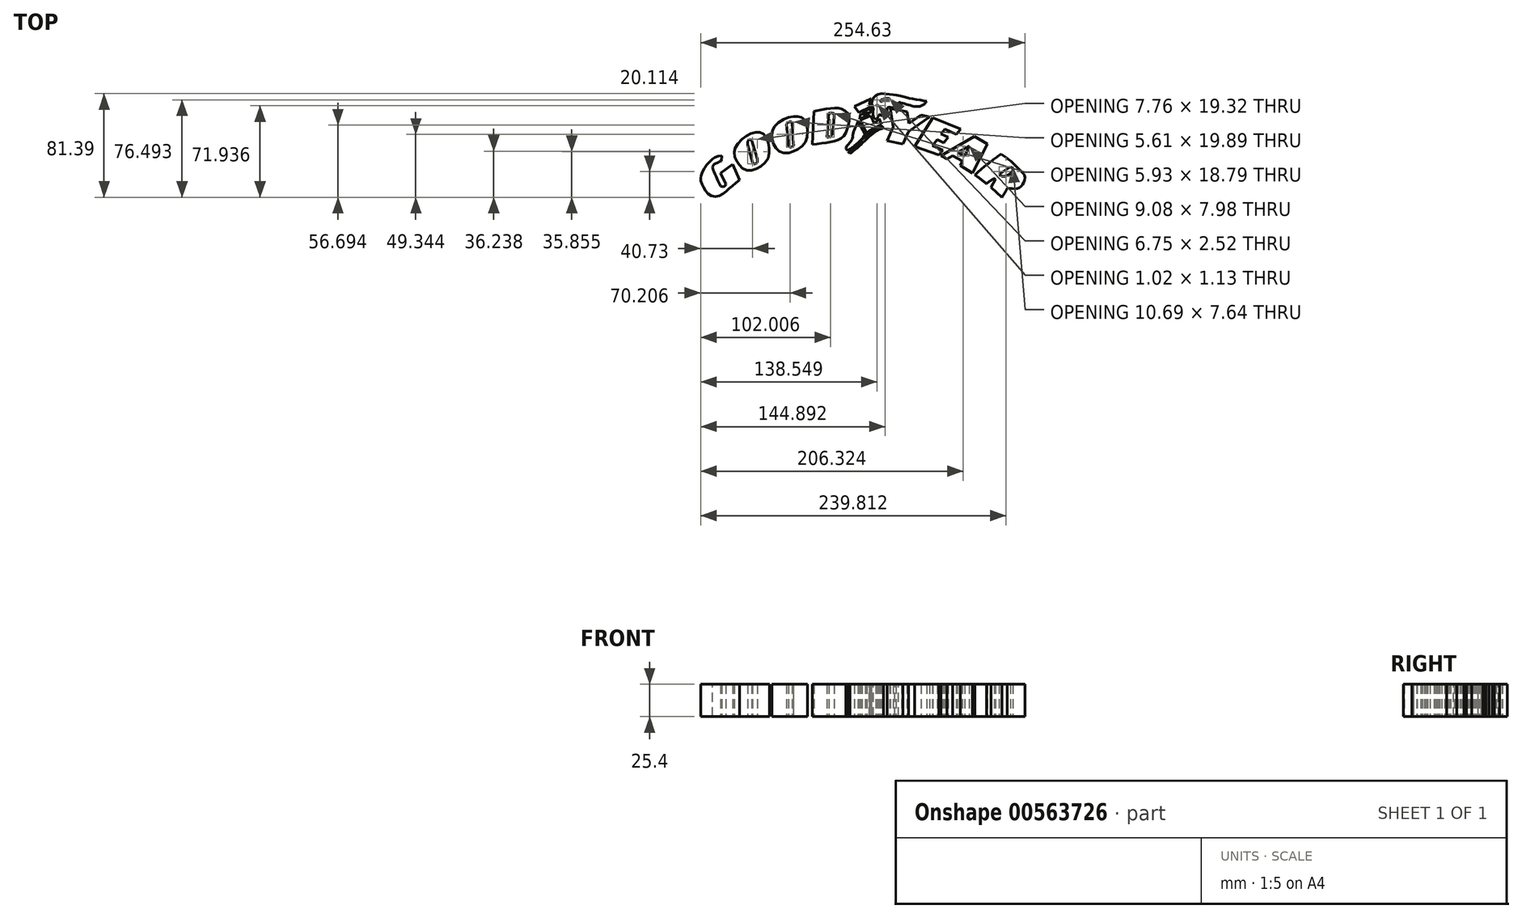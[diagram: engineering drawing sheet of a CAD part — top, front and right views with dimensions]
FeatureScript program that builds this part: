
annotation { "Feature Type Name" : "Feature", "Feature Type Description" : "" }
export const myFeature = defineFeature(function(context is Context, id is Id, definition is map)
    precondition{}
    {
        {
            var Q0;
            Q0=qCreatedBy(makeId("Top.planeOp"),FACE);
            var sketch = newSketch(context, id + "F0", { "sketchPlane" : qUnion([Q0])});
            skFitSpline(sketch, "E0", {"points": [v(-59.77, 19.65) * mm, v(-63.83, 18.9) * mm, v(-66.56, 17.29) * mm, v(-70.08, 14) * mm, v(-73.2, 9.83) * mm, v(-75.73, 4.75) * mm, v(-76.25, 2.47) * mm, v(-76.18, 0) * mm, v(-74.98, -3.55) * mm, v(-72.37, -7.96) * mm, v(-69.17, -11.16) * mm, v(-64.56, -12.56) * mm, v(-59.15, -10.76) * mm, v(-55.35, -7.59) * mm, v(-51.14, -3.95) * mm, v(-45.8, 0.36) * mm], "startDerivative": vector(-48.72, 2.07) * mm, "endDerivative": vector(63.75, 50.3) * mm});
            skLineSegment(sketch, "E1", {"start": v(-59.77, 19.65) * mm, "end": v(-59.86, 15.48) * mm});
            skLineSegment(sketch, "E2", {"start": v(-45.8, 0.36) * mm, "end": v(-51.25, 12.96) * mm});
            skLineSegment(sketch, "E3", {"start": v(-51.25, 12.96) * mm, "end": v(-60.63, 5.88) * mm});
            skLineSegment(sketch, "E4", {"start": v(-60.63, 5.88) * mm, "end": v(-56.41, -2.7) * mm});
            skFitSpline(sketch, "E5", {"points": [v(-59.86, 15.48) * mm, v(-62.4, 14.45) * mm, v(-64.42, 13.43) * mm, v(-66.28, 12.15) * mm, v(-66.87, 9.93) * mm, v(-66.03, 7.47) * mm, v(-64, 2.8) * mm, v(-62.32, -0.84) * mm, v(-61.06, -3.39) * mm, v(-60.55, -4.32) * mm, v(-58.95, -4.91) * mm, v(-57.09, -4.06) * mm, v(-56.41, -2.7) * mm], "startDerivative": vector(-29.78, -11.35) * mm, "endDerivative": vector(6.97, 21.82) * mm});
            skFitSpline(sketch, "E6", {"points": [v(-49.9, 22.3) * mm, v(-48.7, 26.42) * mm, v(-44.08, 32.4) * mm, v(-38.41, 36.27) * mm, v(-33.27, 38.01) * mm, v(-29.32, 37.9) * mm, v(-25.5, 35.12) * mm, v(-23.13, 29.56) * mm, v(-22.34, 23.86) * mm, v(-23.27, 17.75) * mm, v(-27.62, 12.43) * mm, v(-32.9, 9.1) * mm, v(-38.3, 7.89) * mm, v(-43.44, 9.73) * mm, v(-46.87, 13.56) * mm, v(-48.97, 17.14) * mm, v(-49.9, 22.3) * mm]});
            skLineSegment(sketch, "E7", {"start": v(-36.05, 31.72) * mm, "end": v(-31.85, 16.84) * mm});
            skLineSegment(sketch, "E8", {"start": v(-39.36, 28.04) * mm, "end": v(-35.4, 14.58) * mm});
            skFitSpline(sketch, "E9", {"points": [v(-39.36, 28.04) * mm, v(-39.36, 30.3) * mm, v(-38.28, 31.96) * mm, v(-36.88, 32.38) * mm, v(-36.05, 31.72) * mm], "startDerivative": vector(-0.89, 7.93) * mm, "endDerivative": vector(3.61, -4.33) * mm});
            skFitSpline(sketch, "E10", {"points": [v(-31.85, 16.84) * mm, v(-31.85, 14.17) * mm, v(-33.09, 13.34) * mm, v(-34.41, 13.08) * mm, v(-35.4, 14.58) * mm], "startDerivative": vector(1.44, -10.29) * mm, "endDerivative": vector(-1.3, 7.85) * mm});
            skLineSegment(sketch, "E11", {"start": v(-8.9, 44.2) * mm, "end": v(-7.35, 27.45) * mm});
            skLineSegment(sketch, "E12", {"start": v(-4.4, 45.2) * mm, "end": v(-3.4, 28.77) * mm});
            skFitSpline(sketch, "E13", {"points": [v(-8.9, 44.2) * mm, v(-8.13, 45.2) * mm, v(-6.65, 46.05) * mm, v(-5.18, 46.05) * mm, v(-4.4, 45.2) * mm], "startDerivative": vector(2.8, 4.36) * mm, "endDerivative": vector(2.83, -4.51) * mm});
            skFitSpline(sketch, "E14", {"points": [v(-7.35, 27.45) * mm, v(-6.5, 26.52) * mm, v(-5.65, 26.29) * mm, v(-4.64, 26.44) * mm, v(-3.4, 27.3) * mm, v(-3.4, 28.77) * mm], "startDerivative": vector(3.78, -5) * mm, "endDerivative": vector(-0.95, 4.32) * mm});
            skFitSpline(sketch, "E15", {"points": [v(-18.2, 42.64) * mm, v(-12.62, 47.37) * mm, v(-6.27, 49.93) * mm, v(-1.3, 50.4) * mm, v(2.34, 49.85) * mm, v(5.9, 47.3) * mm, v(7.53, 39.7) * mm, v(6.83, 32.33) * mm, v(4.12, 27.53) * mm, v(-1.46, 23.89) * mm, v(-6.11, 21.87) * mm, v(-12.23, 22.1) * mm, v(-16.34, 24.5) * mm, v(-18.82, 28.46) * mm, v(-20.22, 33.88) * mm, v(-19.9, 39.39) * mm, v(-18.2, 42.64) * mm]});
            skLineSegment(sketch, "E16", {"start": v(11.4, 28.26) * mm, "end": v(12.75, 54.33) * mm});
            skFitSpline(sketch, "E17", {"points": [v(12.75, 54.33) * mm, v(20.03, 55.86) * mm, v(28.5, 57.04) * mm, v(34.08, 56.36) * mm, v(39.5, 52.64) * mm, v(40.17, 45.53) * mm, v(38.14, 38.42) * mm, v(34.59, 33.68) * mm, v(28.83, 31.14) * mm, v(21.05, 29.62) * mm, v(11.4, 28.26) * mm], "startDerivative": vector(68.9, 15.11) * mm, "endDerivative": vector(-84.89, -11.4) * mm});
            skLineSegment(sketch, "E18", {"start": v(24.6, 52.98) * mm, "end": v(22.74, 34.19) * mm});
            skFitSpline(sketch, "E19", {"points": [v(24.6, 52.98) * mm, v(27.14, 52.98) * mm, v(28.44, 52.5) * mm, v(28.64, 50.15) * mm, v(27.66, 41.03) * mm, v(26.74, 36.1) * mm, v(26.16, 35.14) * mm, v(25.17, 34.46) * mm, v(22.74, 34.19) * mm], "startDerivative": vector(22.33, 0.87) * mm, "endDerivative": vector(-23, -0.54) * mm});
            skFitSpline(sketch, "E20", {"points": [v(39.1, 23.6) * mm, v(44.18, 27) * mm, v(48.7, 31.12) * mm, v(50.89, 33.22) * mm, v(51.7, 34.88) * mm, v(52.92, 36) * mm], "startDerivative": vector(19.7, 11.7) * mm, "endDerivative": vector(13.38, 3.84) * mm});
            skLineSegment(sketch, "E21", {"start": v(47.46, 46.57) * mm, "end": v(52.92, 36) * mm});
            skFitSpline(sketch, "E22", {"points": [v(47.46, 46.57) * mm, v(46.54, 44.19) * mm, v(45.11, 41.5) * mm, v(43.53, 37) * mm, v(42.43, 32.07) * mm, v(39.8, 28.44) * mm, v(38.07, 26.31) * mm, v(37.96, 24.84) * mm, v(39.1, 23.6) * mm], "startDerivative": vector(-7.2, -21.21) * mm, "endDerivative": vector(15.31, -12.42) * mm});
            skLineSegment(sketch, "E23", {"start": v(40.96, 21.31) * mm, "end": v(39.53, 22.69) * mm});
            skLineSegment(sketch, "E24", {"start": v(65.88, 43.08) * mm, "end": v(67.2, 41.3) * mm});
            skFitSpline(sketch, "E25", {"points": [v(65.88, 43.08) * mm, v(64.37, 42.22) * mm, v(62.42, 41.22) * mm, v(59.63, 39.5) * mm, v(56.94, 37.62) * mm, v(53.71, 35.18) * mm, v(48.96, 30.47) * mm, v(47.97, 29.32) * mm, v(46.11, 27.54) * mm, v(43.82, 25.45) * mm, v(41.44, 24.06) * mm, v(39.53, 22.69) * mm], "startDerivative": vector(-17.38, -20) * mm, "endDerivative": vector(-22.35, -17.46) * mm});
            skFitSpline(sketch, "E26", {"points": [v(67.2, 41.3) * mm, v(66, 40.84) * mm, v(64.5, 40.51) * mm, v(62.4, 39.36) * mm, v(58.05, 36.12) * mm, v(53.94, 32.64) * mm, v(49.63, 28.21) * mm, v(46.94, 25.96) * mm, v(44.17, 23.59) * mm, v(40.96, 21.31) * mm], "startDerivative": vector(-16.72, -16.2) * mm, "endDerivative": vector(-28.08, -18.76) * mm});
            skLineSegment(sketch, "E27", {"start": v(47.81, 53.38) * mm, "end": v(44.5, 58.28) * mm});
            skLineSegment(sketch, "E28", {"start": v(44.5, 58.28) * mm, "end": v(57.43, 64.4) * mm});
            skLineSegment(sketch, "E29", {"start": v(47.81, 53.38) * mm, "end": v(57.06, 57.79) * mm});
            skFitSpline(sketch, "E30", {"points": [v(57.43, 64.4) * mm, v(56.51, 62.01) * mm, v(56.51, 59.2) * mm, v(57.06, 57.79) * mm], "startDerivative": vector(-3.12, -6.33) * mm, "endDerivative": vector(2.33, -4.57) * mm});
            skLineSegment(sketch, "E31", {"start": v(50.63, 53.74) * mm, "end": v(57.69, 57.09) * mm});
            skLineSegment(sketch, "E32", {"start": v(50.63, 53.74) * mm, "end": v(57.3, 53.2) * mm});
            skFitSpline(sketch, "E33", {"points": [v(57.69, 57.09) * mm, v(57.17, 55.72) * mm, v(57.3, 53.2) * mm], "startDerivative": vector(-2.15, -4.28) * mm, "endDerivative": vector(1.5, -3.48) * mm});
            skLineSegment(sketch, "E34", {"start": v(48.55, 48.32) * mm, "end": v(49.17, 52.19) * mm});
            skLineSegment(sketch, "E35", {"start": v(49.17, 52.19) * mm, "end": v(56.3, 51.91) * mm});
            skLineSegment(sketch, "E36", {"start": v(48.55, 48.32) * mm, "end": v(56.3, 51.91) * mm});
            skLineSegment(sketch, "E37", {"start": v(48.94, 47.29) * mm, "end": v(54.3, 36.9) * mm});
            skLineSegment(sketch, "E38", {"start": v(48.94, 47.29) * mm, "end": v(57.19, 51.08) * mm});
            skLineSegment(sketch, "E39", {"start": v(57.19, 51.08) * mm, "end": v(58.36, 48.52) * mm});
            skFitSpline(sketch, "E40", {"points": [v(58.36, 48.52) * mm, v(59.08, 46.84) * mm, v(59.66, 45.79) * mm, v(61.14, 45.98) * mm, v(63.83, 48.86) * mm], "startDerivative": vector(3.27, -7.15) * mm, "endDerivative": vector(7.57, 10.06) * mm});
            skLineSegment(sketch, "E41", {"start": v(63.83, 48.86) * mm, "end": v(65.82, 44.11) * mm});
            skFitSpline(sketch, "E42", {"points": [v(54.3, 36.9) * mm, v(55.69, 38.57) * mm, v(60.65, 41.48) * mm, v(65.82, 44.11) * mm], "startDerivative": vector(4.45, 7) * mm, "endDerivative": vector(13.02, 6.62) * mm});
            skFitSpline(sketch, "E43", {"points": [v(61.18, 48.14) * mm, v(59.75, 49.36) * mm, v(58.81, 53.55) * mm, v(59.36, 56.2) * mm, v(58.43, 58.46) * mm, v(58.43, 62.76) * mm, v(60.3, 66.01) * mm, v(63.28, 67.89) * mm, v(68.08, 68.22) * mm, v(73.92, 67.61) * mm, v(78.94, 66.95) * mm, v(86.83, 64.74) * mm, v(91.57, 63.97) * mm, v(97.08, 63.03) * mm, v(101.33, 62.43) * mm], "startDerivative": vector(-31.99, 17.8) * mm, "endDerivative": vector(56.5, -7.36) * mm});
            skFitSpline(sketch, "E44", {"points": [v(101.33, 62.43) * mm, v(98.46, 59.34) * mm, v(94.1, 58.18) * mm, v(88.87, 58.9) * mm, v(84.12, 60.28) * mm, v(81.15, 61.1) * mm, v(79.88, 61.54) * mm, v(79.16, 60.94) * mm, v(79.71, 60.39) * mm, v(80.65, 59.9) * mm, v(81.75, 59.72) * mm], "startDerivative": vector(-19.3, -26.52) * mm, "endDerivative": vector(16.87, -1.16) * mm});
            skFitSpline(sketch, "E45", {"points": [v(81.75, 59.72) * mm, v(79.88, 58.68) * mm, v(78, 58.73) * mm, v(76.46, 58.95) * mm, v(76.4, 58.24) * mm, v(77.18, 57.85) * mm], "startDerivative": vector(-7.43, -5.2) * mm, "endDerivative": vector(5.92, -1.38) * mm});
            skFitSpline(sketch, "E46", {"points": [v(77.18, 57.85) * mm, v(76.35, 57.32) * mm, v(74.43, 57.29) * mm, v(72.68, 57.62) * mm, v(70.63, 57.45) * mm, v(70.2, 54.94) * mm, v(69.4, 53.45) * mm, v(67.58, 53.5) * mm, v(66.48, 51.67) * mm, v(65.59, 51) * mm, v(64.36, 51.84) * mm, v(63.05, 50.4) * mm, v(62.37, 48.62) * mm, v(61.18, 48.14) * mm], "startDerivative": vector(-11.9, -10.87) * mm, "endDerivative": vector(-16.98, 9.93) * mm});
            skFitSpline(sketch, "E47", {"points": [v(61.74, 59.24) * mm, v(62.63, 59.24) * mm, v(62.65, 58.37) * mm, v(62.19, 58.35) * mm, v(62.32, 58.84) * mm, v(61.9, 58.82) * mm, v(61.74, 59.24) * mm]});
            skFitSpline(sketch, "E48", {"points": [v(65.21, 62.9) * mm, v(66.4, 63.76) * mm, v(68.44, 64.34) * mm, v(70.3, 64.56) * mm, v(71.94, 64.47) * mm, v(71.87, 63.65) * mm, v(69.29, 63.25) * mm, v(66.9, 62.78) * mm, v(66.02, 62.18) * mm, v(65.15, 62.25) * mm, v(65.21, 62.9) * mm]});
            skLineSegment(sketch, "E49", {"start": v(72.66, 56.7) * mm, "end": v(75.06, 41.97) * mm});
            skLineSegment(sketch, "E50", {"start": v(75.06, 41.97) * mm, "end": v(70.23, 31.2) * mm});
            skLineSegment(sketch, "E51", {"start": v(70.23, 31.2) * mm, "end": v(82.54, 28.69) * mm});
            skLineSegment(sketch, "E52", {"start": v(82.54, 28.69) * mm, "end": v(87, 38.62) * mm});
            skLineSegment(sketch, "E53", {"start": v(87, 38.62) * mm, "end": v(103.68, 50.06) * mm});
            skLineSegment(sketch, "E54", {"start": v(103.68, 50.06) * mm, "end": v(96.8, 51.47) * mm});
            skLineSegment(sketch, "E55", {"start": v(96.8, 51.47) * mm, "end": v(87.33, 44.97) * mm});
            skLineSegment(sketch, "E56", {"start": v(87.33, 44.97) * mm, "end": v(85.86, 54) * mm});
            skLineSegment(sketch, "E57", {"start": v(85.86, 54) * mm, "end": v(72.66, 56.7) * mm});
            skLineSegment(sketch, "E58", {"start": v(91.9, 26.82) * mm, "end": v(106.1, 49.42) * mm});
            skLineSegment(sketch, "E59", {"start": v(106.1, 49.42) * mm, "end": v(128.08, 40.3) * mm});
            skLineSegment(sketch, "E60", {"start": v(128.08, 40.3) * mm, "end": v(124.49, 36.46) * mm});
            skLineSegment(sketch, "E61", {"start": v(124.49, 36.46) * mm, "end": v(115.55, 40.57) * mm});
            skLineSegment(sketch, "E62", {"start": v(115.55, 40.57) * mm, "end": v(112.49, 36.8) * mm});
            skLineSegment(sketch, "E63", {"start": v(112.49, 36.8) * mm, "end": v(118.1, 34.18) * mm});
            skLineSegment(sketch, "E64", {"start": v(118.1, 34.18) * mm, "end": v(114.68, 29.54) * mm});
            skLineSegment(sketch, "E65", {"start": v(114.68, 29.54) * mm, "end": v(109.42, 32.16) * mm});
            skLineSegment(sketch, "E66", {"start": v(109.42, 32.16) * mm, "end": v(105.74, 27.43) * mm});
            skLineSegment(sketch, "E67", {"start": v(105.74, 27.43) * mm, "end": v(114.15, 24.02) * mm});
            skLineSegment(sketch, "E68", {"start": v(114.15, 24.02) * mm, "end": v(110.82, 20) * mm});
            skLineSegment(sketch, "E69", {"start": v(110.82, 20) * mm, "end": v(91.9, 26.82) * mm});
            skLineSegment(sketch, "E70", {"start": v(112.29, 19.53) * mm, "end": v(138.65, 34.6) * mm});
            skLineSegment(sketch, "E71", {"start": v(138.65, 34.6) * mm, "end": v(149.02, 28.7) * mm});
            skLineSegment(sketch, "E72", {"start": v(149.02, 28.7) * mm, "end": v(137.16, 5.95) * mm});
            skLineSegment(sketch, "E73", {"start": v(137.16, 5.95) * mm, "end": v(127.55, 11.85) * mm});
            skLineSegment(sketch, "E74", {"start": v(127.55, 11.85) * mm, "end": v(129.33, 15.35) * mm});
            skLineSegment(sketch, "E75", {"start": v(129.33, 15.35) * mm, "end": v(121.52, 19.59) * mm});
            skLineSegment(sketch, "E76", {"start": v(121.52, 19.59) * mm, "end": v(117.2, 16.87) * mm});
            skLineSegment(sketch, "E77", {"start": v(117.2, 16.87) * mm, "end": v(112.29, 19.53) * mm});
            skLineSegment(sketch, "E78", {"start": v(125.49, 22.15) * mm, "end": v(134.56, 27.12) * mm});
            skLineSegment(sketch, "E79", {"start": v(134.56, 27.12) * mm, "end": v(131.04, 19.14) * mm});
            skLineSegment(sketch, "E80", {"start": v(131.04, 19.14) * mm, "end": v(125.49, 22.15) * mm});
            skFitSpline(sketch, "E81", {"points": [v(139.14, 4.57) * mm, v(145.18, 9.89) * mm, v(153.62, 16.45) * mm, v(159.77, 20.93) * mm], "startDerivative": vector(17.67, 16.08) * mm, "endDerivative": vector(18.73, 13.48) * mm});
            skFitSpline(sketch, "E82", {"points": [v(159.77, 20.93) * mm, v(168.42, 14.37) * mm, v(174.98, 7.8) * mm, v(178.1, 3.84) * mm, v(177.07, -2.4) * mm, v(172.06, -6.16) * mm, v(164.56, -5.74) * mm], "startDerivative": vector(44.5, -30.97) * mm, "endDerivative": vector(-46.73, 8.55) * mm});
            skFitSpline(sketch, "E83", {"points": [v(164.56, -5.74) * mm, v(162.69, -9.4) * mm, v(160.38, -13.1) * mm], "startDerivative": vector(-3.62, -7.3) * mm, "endDerivative": vector(-4.1, -6.66) * mm});
            skFitSpline(sketch, "E84", {"points": [v(139.14, 4.57) * mm, v(143.4, 1.34) * mm, v(148.2, -2.4) * mm], "startDerivative": vector(8.71, -6.53) * mm, "endDerivative": vector(9.4, -7.42) * mm});
            skFitSpline(sketch, "E85", {"points": [v(148.2, -2.4) * mm, v(150.73, -0.48) * mm, v(154.35, 1.86) * mm], "startDerivative": vector(4.88, 2.85) * mm, "endDerivative": vector(7.3, 5.55) * mm});
            skLineSegment(sketch, "E86", {"start": v(154.35, 1.86) * mm, "end": v(155.3, 1.04) * mm});
            skLineSegment(sketch, "E87", {"start": v(155.3, 1.04) * mm, "end": v(151.65, -5.27) * mm});
            skLineSegment(sketch, "E88", {"start": v(151.65, -5.27) * mm, "end": v(160.38, -13.1) * mm});
            skLineSegment(sketch, "E89", {"start": v(158.17, 4.93) * mm, "end": v(167, 10.82) * mm});
            skFitSpline(sketch, "E90", {"points": [v(167, 10.82) * mm, v(168.9, 9.08) * mm, v(167.83, 6.42) * mm, v(164.02, 3.8) * mm, v(161.31, 3.23) * mm, v(158.17, 4.93) * mm], "startDerivative": vector(14.19, -8.55) * mm, "endDerivative": vector(-15.28, 10.77) * mm});
            skSolve(sketch);
        }
        {
            var Q0;
            Q0 = qSketchRegion(id + "F0", true);
            extrude(context, id + "F1", {"entities" : qUnion([Q0]), "depth" : 25.4 * mm, "offsetDistance" : 25.4 * mm});
        }
    });
